# Revit family: rba-bim-rba8302-340
name_source: partatom
category: Plumbing Fixtures
revit_build: Autodesk Revit 2015 (Build: 20140223_1515(x64)
units: mm (PartAtom-declared; Revit-internal decimal feet)

## types (1)
- rba8302-340
    Amperage = 0
    CW Connection = No
    CWFU = 0
    Default Elevation = 0 mm  [stored 0 ft]
    Description = Combination Station, Plastic Bowl Eyewash and Showerhead
Eye/Face Wash and Showerhea
    HW Connection = No
    HWFU = 0
    Manufacturer = RBA Group
    Material = Stainless Steel
    Material Eye/Face Wash = Plastic ABS Yellow
    Model = rba8302-340
    Modified Issue = 20160518 $
    Tempered Water Connection = Yes
    URL = http://www.rba.com.au
    Vent Connection = No
    Voltage = 0
    WFU = 0
    Waste Connection = Yes

note: [stored X ft] marks values corroborated as IEEE doubles in the binary element streams (Revit-internal decimal feet)

## geometry (parser evidence)
native form markers: Sweep x4
no freeform markers — native parametric forms only
